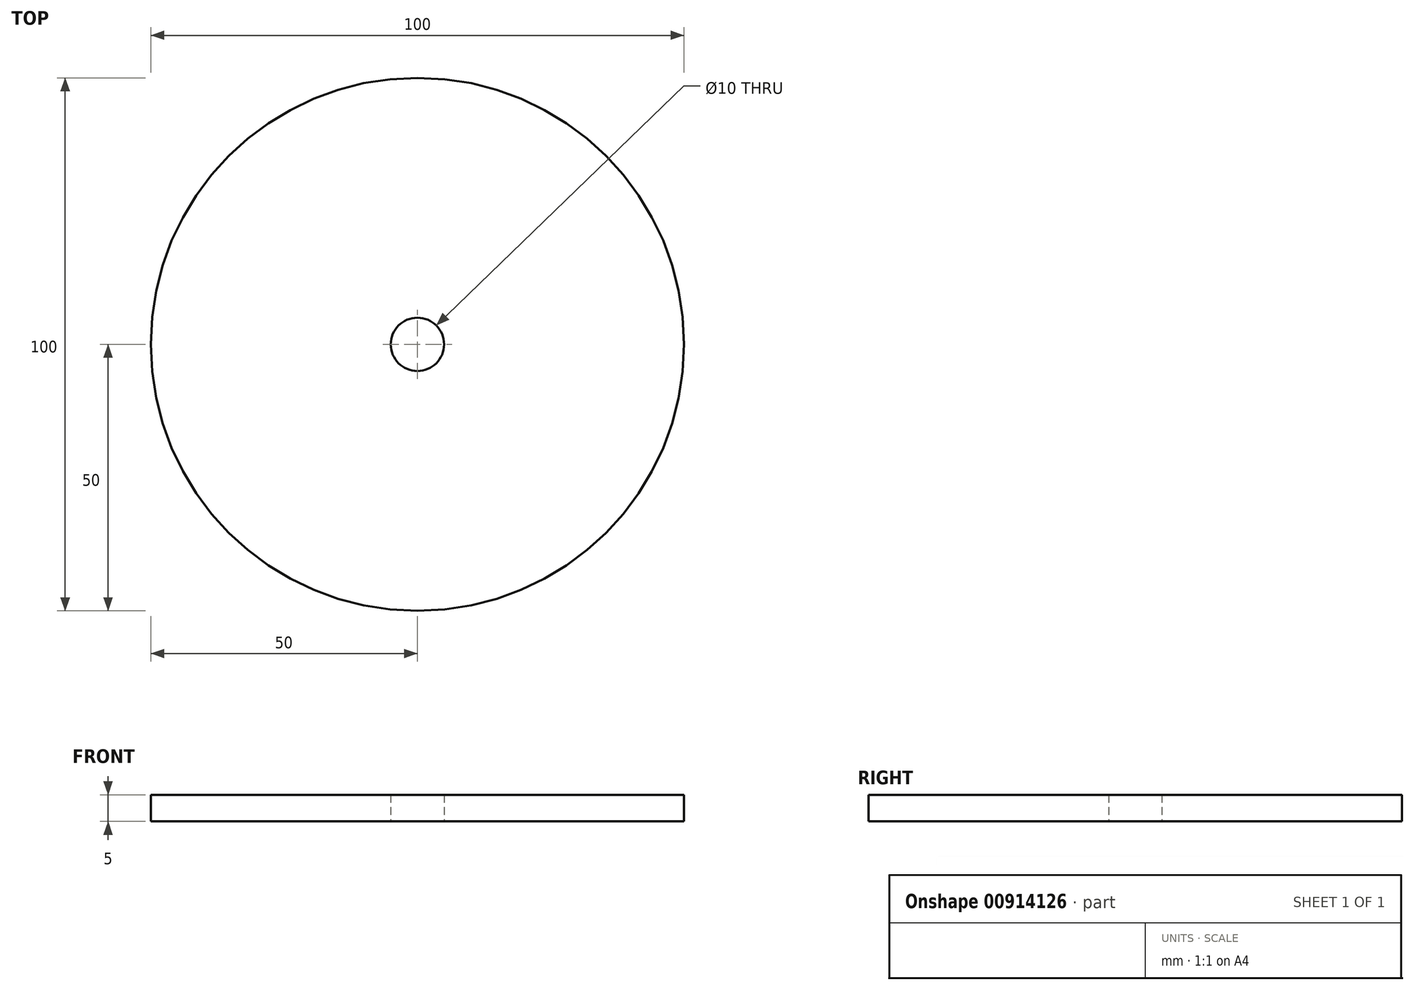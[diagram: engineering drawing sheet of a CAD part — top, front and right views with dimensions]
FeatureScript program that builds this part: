
annotation { "Feature Type Name" : "Feature", "Feature Type Description" : "" }
export const myFeature = defineFeature(function(context is Context, id is Id, definition is map)
    precondition{}
    {
        {
            var Q0;
            Q0=qCreatedBy(makeId("Top.planeOp"),FACE);
            var sketch = newSketch(context, id + "F0", { "sketchPlane" : qUnion([Q0])});
            skCircle(sketch, "E0", {"center": v(0, 0) * mm, "radius": 50 * mm});
            skCircle(sketch, "E1", {"center": v(0, 0) * mm, "radius": 5 * mm});
            skSolve(sketch);
        }
        {
            var Q0;
            Q0=makeQuery(id+"F0.imprint","IMPRINT",FACE,{"disambiguationData":[TD([[makeQuery(id+"F0.imprint","IMPRINT",EDGE,{"derivedFrom":sQuery(id+"F0.wireOp",EDGE,"E0")}),1.0]])]});
            extrude(context, id + "F1", {"entities" : qUnion([Q0]), "depth" : 5 * mm, "offsetDistance" : 25 * mm});
        }
    });
